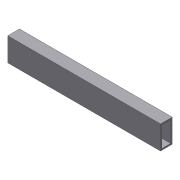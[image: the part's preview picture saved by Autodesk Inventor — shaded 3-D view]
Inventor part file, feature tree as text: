
AUTODESK INVENTOR PART (.ipt)
format: ipt  version: 2012 (Build 160160000, 160)  size: 72,704 bytes
history: native  units: in
note: dims shown in document units (in); Inventor stores cm internally (conversion verified against a paired STEP export)
features: extrude x1, shell x1, sketch x1
ambient origin geometry x8: Origin, YZ Plane, XZ Plane, XY Plane, X Axis, Y Axis, Z Axis, Center Point
bodies: Solid1 (feature_tree)
feature tree (3):
  extrude  "Extrusion1"  Depth=2.0in
  shell  "Shell1"  Thickness=1.0in
  sketch  "Sketch1"  dims[d0=13.0in d1=2.0in d2=1.0in d3=0.0in d4=0.125in]
